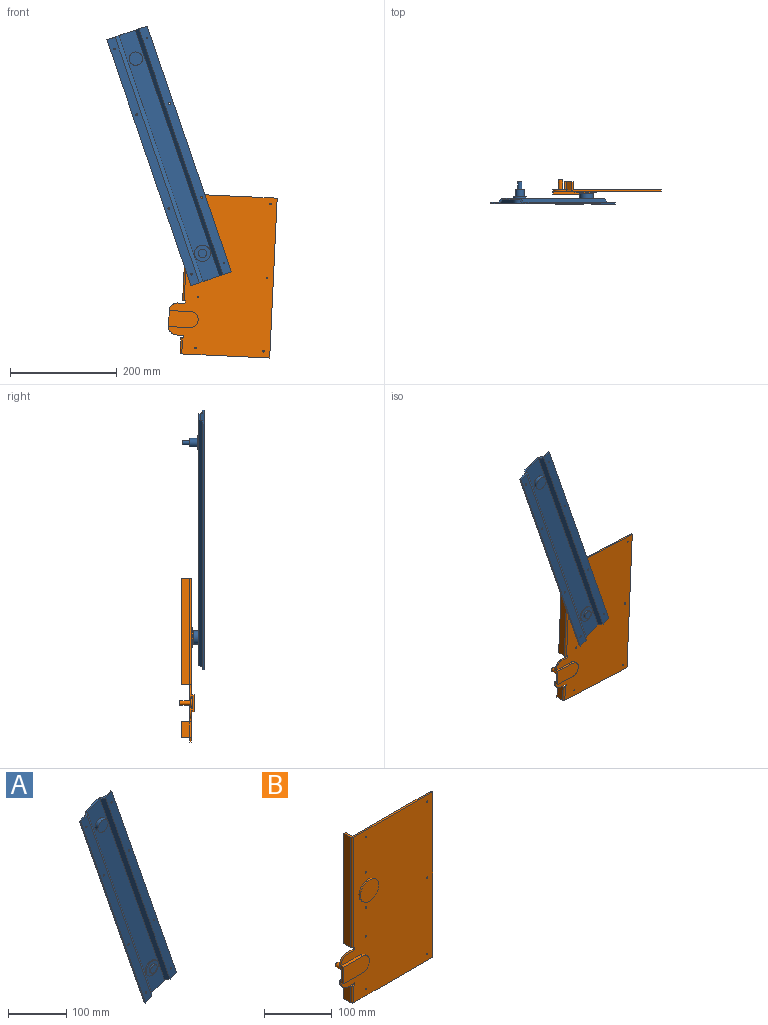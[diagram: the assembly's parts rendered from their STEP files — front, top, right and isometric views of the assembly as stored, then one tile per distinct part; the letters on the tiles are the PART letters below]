
ASSEMBLY  parts=2 mates=1
PART A: 38 faces, bbox 233.3x41x486.7 mm
  f0: plane 466.12x173.26mm, normal (0,-1,0), area 8003.3mm2, adj f2,f11,f12,f13,f17,f18,f19,f21
  f1: plane 466.12x173.26mm, normal (0,-1,0), area 8003.5mm2, adj f4,f5,f12,f13,f14,f15,f16,f20
  f2: plane 463.04x164.27mm, normal (0.67,-0.71,0.23), area 4821.1mm2, adj f0,f3,f12,f13
  f3: plane 471.47x188.88mm, normal (0,-1,0), area 14873.5mm2, adj f2,f4,f12,f13,f26,f32
  f4: plane 463.05x164.27mm, normal (-0.67,-0.71,-0.23), area 4820.7mm2, adj f1,f3,f12,f13
  f5: plane 460.78x157.64mm, normal (0.95,0,0.32), area 1461mm2, adj f1,f6,f12,f13
  f6: plane 465.64x171.84mm, normal (0,1,0), area 7272.6mm2, adj f5,f7,f12,f13,f14,f15,f16,f20
  f7: plane 463.05x164.27mm, normal (0.67,0.71,0.23), area 4821.1mm2, adj f6,f8,f12,f13
  f8: plane 472.44x191.71mm, normal (0,1,0), area 16550.2mm2, adj f7,f9,f12,f13,f23,f31
  f9: plane 463.04x164.27mm, normal (-0.67,0.71,-0.23), area 4821.1mm2, adj f8,f10,f12,f13
  f10: plane 465.64x171.84mm, normal (0,1,0), area 7272.9mm2, adj f9,f11,f12,f13,f17,f18,f19,f21
  f11: plane 460.78x157.64mm, normal (-0.95,0,-0.32), area 1461mm2, adj f0,f10,f12,f13
  f12: plane 75.69x25.9mm, normal (-0.32,0,0.95), area 261mm2, adj f0,f1,f2,f3,f4,f5,f6,f7
  f13: plane 75.69x25.9mm, normal (0.32,0,-0.95), area 261mm2, adj f0,f1,f2,f3,f4,f5,f6,f7
  f14: cylinder r=1.6mm len=3.2mm, axis (0,-1,0), area 30.2mm2, adj f1,f6
  f15: cylinder r=1.6mm len=3.2mm, axis (0,-1,0), area 30.2mm2, adj f1,f6
  f16: cylinder r=1.6mm len=3.2mm, axis (0,-1,0), area 30.2mm2, adj f1,f6
  f17: cylinder r=1.6mm len=3.2mm, axis (0,-1,0), area 30.2mm2, adj f0,f10
  f18: cylinder r=1.6mm len=3.2mm, axis (0,-1,0), area 30.2mm2, adj f0,f10
  f19: cylinder r=1.6mm len=3.2mm, axis (0,-1,0), area 30.2mm2, adj f0,f10
  f20: cylinder r=1.6mm len=3.2mm, axis (0,-1,0), area 30.2mm2, adj f1,f6
  f21: cylinder r=1.6mm len=3.2mm, axis (0,-1,0), area 30.2mm2, adj f0,f10
  f22: plane 25x25mm, normal (0,1,0), area 412.3mm2, adj f23,f25
  f23: cylinder r=12.5mm len=25mm, axis (0,-1,0), area 785mm2, adj f8,f22
  f24: plane 10x10mm, normal (0,1,0), area 78.6mm2, adj f25
  f25: cylinder r=5mm len=10mm, axis (0,-1,0), area 157.1mm2, adj f22,f24
  f26: cylinder r=15mm len=30mm, axis (0,-1,0), area 189mm2, adj f3,f27
  f27: plane 30x30mm, normal (0,-1,0), area 505.8mm2, adj f26,f28
  f28: cylinder r=8mm len=16mm, axis (0,-1,0), area 201.1mm2, adj f27,f29
  f29: plane 16x16mm, normal (0,-1,0), area 201.1mm2, adj f28
  f30: plane 25x25mm, normal (0,1,0), area 289.8mm2, adj f31,f37
  f31: cylinder r=12.5mm len=25mm, axis (0,-1,0), area 230.6mm2, adj f8,f30
  f32: cylinder r=12.5mm len=25mm, axis (0,-1,0), area 554.7mm2, adj f3,f33
  f33: plane 25x25mm, normal (0,-1,0), area 490.9mm2, adj f32
  f34: plane 8x8mm, normal (0,1,0), area 50.3mm2, adj f35
  f35: cylinder r=4mm len=14mm, axis (0,-1,0), area 351.9mm2, adj f34,f36
  f36: plane 16x16mm, normal (0,1,0), area 150.8mm2, adj f35,f37
  f37: cylinder r=8mm len=16mm, axis (0,-1,0), area 703.7mm2, adj f30,f36
PART B: 46 faces, bbox 192.2x26.5x300 mm
  f0: plane 40x5mm, normal (0,0,1), area 200mm2, adj f2,f24,f36,f41
  f1: plane 40x5mm, normal (0,0,-1), area 200mm2, adj f2,f24,f36,f41
  f2: cylinder r=12mm len=24mm, axis (0,1,0), area 188.5mm2, adj f0,f1,f24,f41
  f3: cylinder r=16.28mm len=32.57mm, axis (0,1,0), area 307mm2, adj f24,f33
  f4: cylinder r=15.2mm len=15.2mm, axis (0,1,0), area 71mm2, adj f22,f23,f24,f36
  f5: cylinder r=15.2mm len=15.2mm, axis (0,1,0), area 71mm2, adj f6,f23,f24,f36
  f6: plane 13.6x3mm, normal (0,0,-1), area 40.8mm2, adj f5,f7,f23,f24
  f7: plane 5x3mm, normal (-1,0,0), area 15mm2, adj f6,f8,f23,f24
  f8: plane 18x4.59mm, normal (0,0,1), area 56.8mm2, adj f7,f23,f24,f25,f26,f27,f34
  f9: plane 168.01x18mm, normal (0,0,-1), area 547.2mm2, adj f10,f23,f24,f25,f26,f27,f34
  f10: plane 300x3mm, normal (1,0,0), area 900mm2, adj f9,f11,f23,f24
  f11: plane 168.01x18mm, normal (0,0,1), area 547.1mm2, adj f10,f23,f24,f28,f29,f30,f35
  f12: plane 18x4.59mm, normal (0,0,-1), area 56.8mm2, adj f13,f23,f24,f28,f29,f30,f35
  f13: plane 5x3mm, normal (-1,0,0), area 15mm2, adj f12,f22,f23,f24
  f14: cylinder r=1.25mm len=3mm, axis (0,1,0), area 23.6mm2, adj f23,f24
  f15: cylinder r=1.25mm len=3mm, axis (0,1,0), area 23.6mm2, adj f23,f24
  f16: cylinder r=1.25mm len=3mm, axis (0,1,0), area 23.6mm2, adj f23,f24
  f17: cylinder r=1.25mm len=3mm, axis (0,1,0), area 23.6mm2, adj f23,f24
  f18: cylinder r=1.37mm len=3mm, axis (0,1,0), area 25.9mm2, adj f23,f24
  f19: cylinder r=1.37mm len=3mm, axis (0,1,0), area 25.9mm2, adj f23,f24
  f20: cylinder r=1.38mm len=3mm, axis (0,1,0), area 25.9mm2, adj f23,f24
  f21: cylinder r=1.25mm len=3mm, axis (0,1,0), area 23.6mm2, adj f23,f24
  f22: plane 13.6x3mm, normal (0,0,1), area 40.8mm2, adj f4,f13,f23,f24
  f23: plane 300x192.22mm, normal (0,-1,0), area 48257.1mm2, adj f4,f5,f6,f7,f8,f9,f10,f11
  f24: plane 300x192.22mm, normal (0,1,0), area 48959.5mm2, adj f0,f1,f2,f3,f4,f5,f6,f7
  f25: plane 30x15mm, normal (1,0,0), area 450mm2, adj f8,f9,f24,f27
  f26: plane 30x15mm, normal (-1,0,0), area 450mm2, adj f8,f9,f27,f34
  f27: plane 30x3mm, normal (0,1,0), area 90mm2, adj f8,f9,f25,f26
  f28: plane 200x15mm, normal (1,0,0), area 3000mm2, adj f11,f12,f24,f30
  f29: plane 200x15mm, normal (-1,0,0), area 3000mm2, adj f11,f12,f30,f35
  f30: plane 200x3mm, normal (0,1,0), area 600mm2, adj f11,f12,f28,f29
  f31: cylinder r=19.29mm len=38.57mm, axis (0,1,0), area 363.5mm2, adj f23,f32
  f32: plane 38.57x38.57mm, normal (0,-1,0), area 1168.4mm2, adj f31
  f33: plane 32.57x32.57mm, normal (0,1,0), area 833.1mm2, adj f3
  f34: cylinder r=3mm len=30mm, axis (0,0,-1), area 141.4mm2, adj f8,f9,f23,f26
  f35: cylinder r=3mm len=200mm, axis (0,0,-1), area 942.5mm2, adj f11,f12,f23,f29
  f36: plane 30x8mm, normal (-1,0,0), area 120mm2, adj f0,f1,f4,f5,f24,f37,f39,f40
  f37: plane 40x5mm, normal (0,0,-1), area 200mm2, adj f23,f36,f38,f40
  f38: cylinder r=15mm len=30mm, axis (0,1,0), area 235.6mm2, adj f23,f37,f39,f40
  f39: plane 40x5mm, normal (0,0,1), area 200mm2, adj f23,f36,f38,f40
  f40: plane 55x30mm, normal (0,-1,0), area 1553.4mm2, adj f36,f37,f38,f39
  f41: plane 52x24mm, normal (0,1,0), area 985.1mm2, adj f0,f1,f2,f36,f42
  f42: cylinder r=8mm len=16mm, axis (0,1,0), area 201.1mm2, adj f41,f43
  f43: plane 16x16mm, normal (0,1,0), area 150.8mm2, adj f42,f45
  f44: plane 8x8mm, normal (0,1,0), area 50.3mm2, adj f45
  f45: cylinder r=4mm len=19.5mm, axis (0,-1,0), area 490.1mm2, adj f43,f44
PLACE A t=(-6.9,44.05,11.64)mm fixed
PLACE B rot(axis=(0,1,0),2.7deg) t=(-15.7,44.05,13.24)mm
MATE revolute B.f3 <-> A.f26  axis (0,1,0) through (23.1,44.05,201.64)mm
